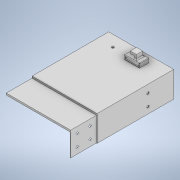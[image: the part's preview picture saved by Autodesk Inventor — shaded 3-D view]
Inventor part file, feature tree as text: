
AUTODESK INVENTOR PART (.ipt)
format: ipt  version: 2021 (Build 250183000, 183)  size: 243,712 bytes
history: native  units: mm
features: sketch x6, extrude x4, projected_geometry x4, other x3, hole x2
ambient origin geometry x8: Origin, YZ Plane, XZ Plane, XY Plane, X Axis, Y Axis, Z Axis, Center Point
bodies: Solid1 (feature_tree)
feature tree (19):
  other  "wallMount.ipt"
  extrude  "Extrusion4"  Depth=10.0mm
  extrude  "Extrusion5"  Depth=1.25mm TaperAngle=0.0deg
  hole  "Hole2"  [1 undecoded]
  extrude  "Extrusion6"  Depth=8.0mm
  hole  "Hole3"  [1 undecoded]
  extrude  "Extrusion7"  [1 undecoded]
  other  "Solid3::wallMount.ipt"
  other  "TaggingFeature1"
  sketch  "Sketch6"  dims[d0=10.0mm d19=25.0mm]
  sketch  "Sketch7"  dims[d20=3.5mm d21=0.0mm d22=1.25mm d23=0.0mm]
  projected_geometry  "Projected Loop2"
  sketch  "Sketch8"  dims[d24=4.5mm d25=6.0mm d26=7.0mm d27=2.0mm d28=90.0deg d29=8.0mm d30=20.594885mm d31=25.0mm d32=0.0mm]
  projected_geometry  "Projected Loop3"
  sketch  "Sketch9"  dims[d33=4.5mm d34=6.0mm d35=7.0mm d36=2.0mm d37=90.0deg d38=8.0mm d39=20.594885mm d40=60.0mm]
  projected_geometry  "Projected Loop4"
  sketch  "Sketch10"  dims[d41=0.0mm d42=0.0mm]
  projected_geometry  "Projected Loop5"
  sketch  "Sketch11"
note: 3 required parameter values undecoded (feature->parameter linkage not recoverable at this tier; creation-order binding heuristic only, values carry confidence <= 0.55)
